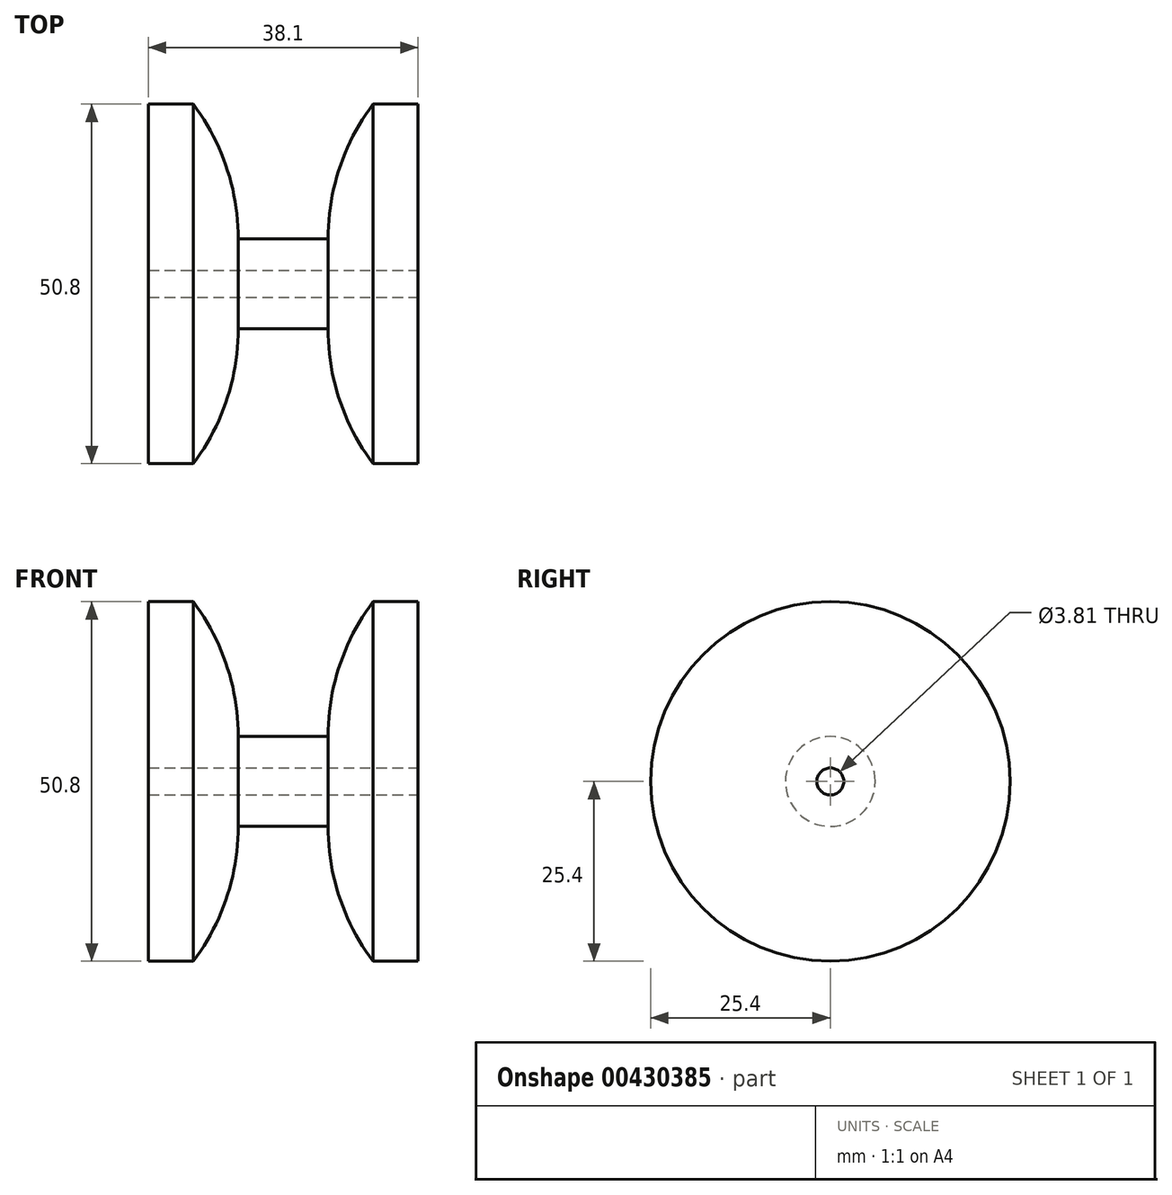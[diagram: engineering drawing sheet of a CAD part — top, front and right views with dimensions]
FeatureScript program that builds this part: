
annotation { "Feature Type Name" : "Feature", "Feature Type Description" : "" }
export const myFeature = defineFeature(function(context is Context, id is Id, definition is map)
    precondition{}
    {
        {
            var Q0;
            Q0=qCreatedBy(makeId("Front.planeOp"),FACE);
            var sketch = newSketch(context, id + "F0", { "sketchPlane" : qUnion([Q0])});
            skLineSegment(sketch, "E0", {"start": v(0, 0) * mm, "end": v(-12.7, 0) * mm});
            skLineSegment(sketch, "E1", {"start": v(-12.7, -12.7) * mm, "end": v(0, -12.7) * mm});
            skLineSegment(sketch, "E2", {"start": v(0, -6.35) * mm, "end": v(6.35, -6.35) * mm});
            skPoint(sketch, "E2.endSnap0", {"position": v(0, -6.35) * mm});
            skArc(sketch, "E3", {"start": v(-19.05, -31.75) * mm, "mid": v(-14.33, -22.74) * mm, "end": v(-12.7, -12.7) * mm});
            skArc(sketch, "E4", {"start": v(0, -12.7) * mm, "mid": v(1.63, -22.74) * mm, "end": v(6.35, -31.75) * mm});
            skArc(sketch, "E5", {"start": v(-12.7, 0) * mm, "mid": v(-14.33, 10.04) * mm, "end": v(-19.05, 19.05) * mm});
            skArc(sketch, "E6", {"start": v(6.35, 19.05) * mm, "mid": v(1.63, 10.04) * mm, "end": v(0, 0) * mm});
            skLineSegment(sketch, "E7", {"start": v(6.35, 19.05) * mm, "end": v(12.7, 19.05) * mm});
            skLineSegment(sketch, "E8", {"start": v(12.7, 19.05) * mm, "end": v(12.7, -31.75) * mm});
            skLineSegment(sketch, "E9", {"start": v(12.7, -31.75) * mm, "end": v(6.35, -31.75) * mm});
            skLineSegment(sketch, "E10", {"start": v(-19.05, -31.75) * mm, "end": v(-25.4, -31.75) * mm});
            skLineSegment(sketch, "E11", {"start": v(-25.4, -31.75) * mm, "end": v(-25.4, 19.05) * mm});
            skLineSegment(sketch, "E12", {"start": v(-25.4, 19.05) * mm, "end": v(-19.05, 19.05) * mm});
            skLineSegment(sketch, "E13", {"start": v(12.7, -6.35) * mm, "end": v(-25.4, -6.35) * mm});
            skSolve(sketch);
        }
        {
            var Q0;
            Q0=makeQuery(id+"F0.imprint","IMPRINT",FACE,{"disambiguationData":[TD([[makeQuery(id+"F0.imprint","IMPRINT",EDGE,{"derivedFrom":sQuery(id+"F0.wireOp",EDGE,"E0")}),1.0]])]});
            var Q1;
            Q1=sQuery(id+"F0.wireOp",EDGE,"E13");
            revolve(context, id + "F1", {"entities" : qUnion([Q0]), "axis" : qUnion([Q1]), "revolveType" : RevolveType.FULL});
        }
        {
            var Q0;
            Q0=makeQuery(id+"F1.opRevolve","SWEPT_FACE",FACE,{"disambiguationData":[OSD([sQuery(id+"F0.wireOp",EDGE,"E8")])]});
            var sketch = newSketch(context, id + "F2", { "sketchPlane" : qUnion([Q0])});
            skLineSegment(sketch, "E14", {"start": v(0, 19.05) * mm, "end": v(0, -6.35) * mm});
            skLineSegment(sketch, "E15", {"start": v(0, -6.35) * mm, "end": v(25.4, -6.35) * mm});
            skCircle(sketch, "E16", {"center": v(0, -6.35) * mm, "radius": 1.9 * mm});
            skSolve(sketch);
        }
        {
            var Q0;
            {var subQ0=sQuery(id+"F2.wireOp",EDGE,"E15");var subQ1=sQuery(id+"F2.wireOp",EDGE,"E14");var subQ2=makeQuery(id+"F2.imprint","INTERSECT",VERTEX,{"derivedFrom":[subQ1,subQ0]});Q0=makeQuery(id+"F2.imprint","IMPRINT",FACE,{"disambiguationData":[TD([[makeQuery(id+"F2.imprint","IMPRINT",EDGE,{"disambiguationData":[TD([[subQ2,1.0]])],"derivedFrom":subQ1}),-1.0]])]});}
            var Q1;
            {var subQ0=sQuery(id+"F2.wireOp",EDGE,"E15");var subQ1=sQuery(id+"F2.wireOp",EDGE,"E14");var subQ2=makeQuery(id+"F2.imprint","INTERSECT",VERTEX,{"derivedFrom":[subQ1,subQ0]});Q1=makeQuery(id+"F2.imprint","IMPRINT",FACE,{"disambiguationData":[TD([[makeQuery(id+"F2.imprint","IMPRINT",EDGE,{"disambiguationData":[TD([[subQ2,1.0]])],"derivedFrom":subQ1}),1.0]])]});}
            extrude(context, id + "F3", {"entities" : qUnion([Q0, Q1]), "operationType" : NewBodyOperationType.REMOVE, "oppositeDirection" : true, "depth" : 101.6 * mm});
        }
    });
